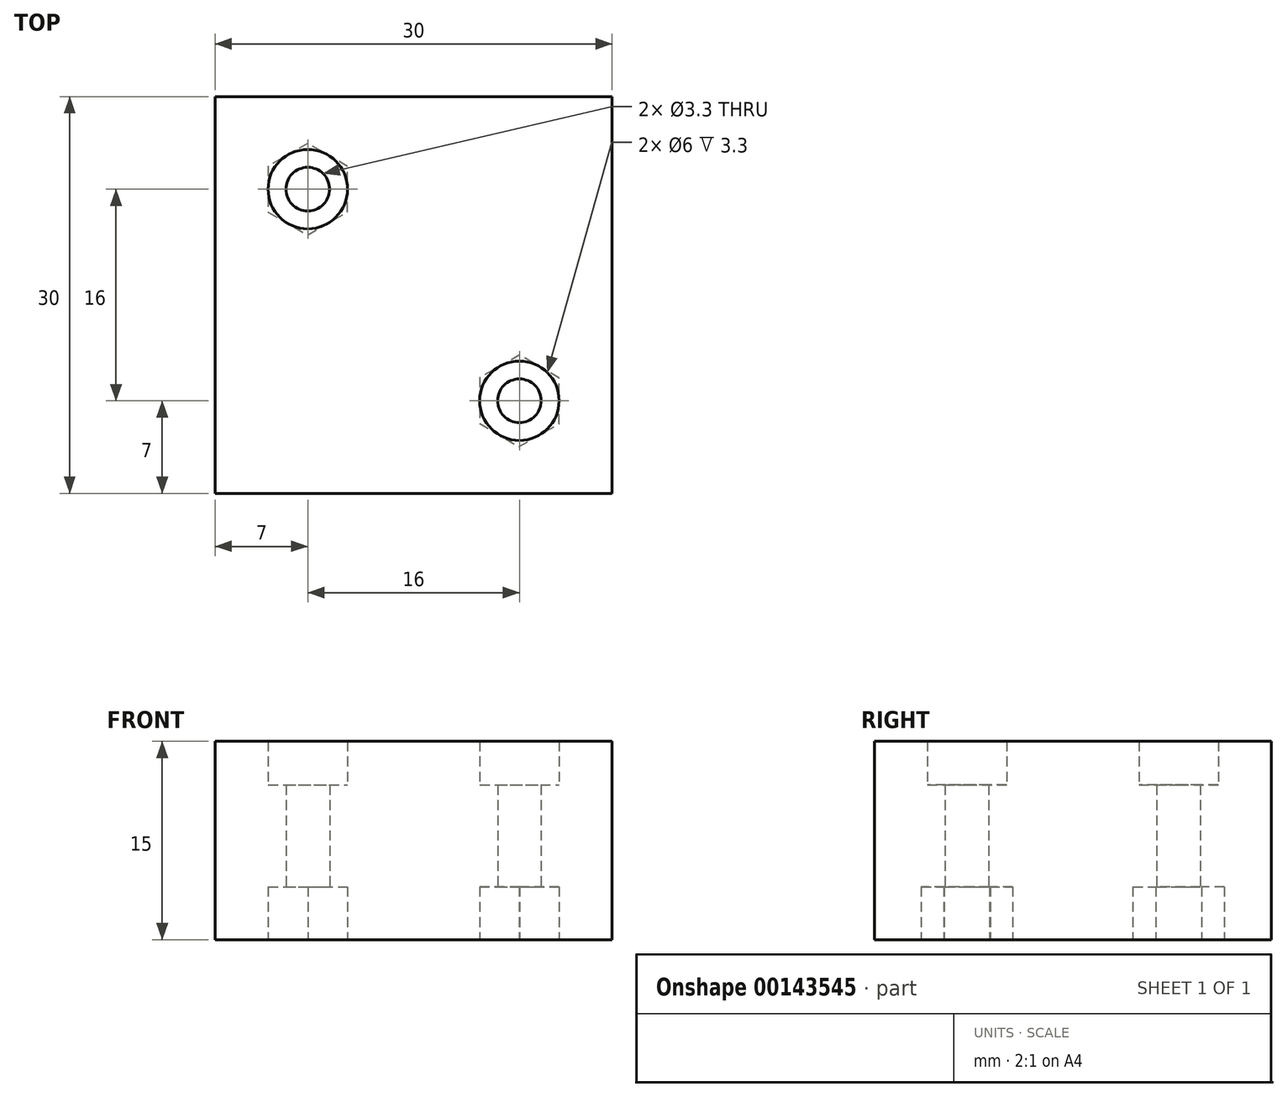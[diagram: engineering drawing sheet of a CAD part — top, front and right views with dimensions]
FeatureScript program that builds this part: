
annotation { "Feature Type Name" : "Feature", "Feature Type Description" : "" }
export const myFeature = defineFeature(function(context is Context, id is Id, definition is map)
    precondition{}
    {
        {
            var Q0;
            Q0=qCreatedBy(makeId("Top.planeOp"),FACE);
            var sketch = newSketch(context, id + "F0", { "sketchPlane" : qUnion([Q0])});
            skLineSegment(sketch, "E0.bottom", {"start": v(-15, 15) * mm, "end": v(15, 15) * mm});
            skLineSegment(sketch, "E0.top", {"start": v(-15, -15) * mm, "end": v(15, -15) * mm});
            skLineSegment(sketch, "E0.left", {"start": v(-15, 15) * mm, "end": v(-15, -15) * mm});
            skLineSegment(sketch, "E0.right", {"start": v(15, 15) * mm, "end": v(15, -15) * mm});
            skSolve(sketch);
        }
        {
            var Q0;
            Q0 = qSketchRegion(id + "F0", true);
            extrude(context, id + "F1", {"entities" : qUnion([Q0]), "depth" : 15 * mm});
        }
        {
            var Q0;
            Q0=makeQuery(id+"F1.opExtrude","CAP_FACE",FACE,{"disambiguationData":[OSD([sQuery(id+"F0.wireOp",EDGE,"E0.bottom"),sQuery(id+"F0.wireOp",EDGE,"E0.top"),sQuery(id+"F0.wireOp",EDGE,"E0.left"),sQuery(id+"F0.wireOp",EDGE,"E0.right")])],"isStart":false});
            var sketch = newSketch(context, id + "F2", { "sketchPlane" : qUnion([Q0])});
            skPoint(sketch, "E1", {"position": v(-8, 8) * mm});
            skPoint(sketch, "E2", {"position": v(8, -8) * mm});
            skSolve(sketch);
        }
        {
            var Q0;
            Q0=sQuery(id+"F2.wireOp",VERTEX,"E1");
            var Q1;
            Q1=sQuery(id+"F2.wireOp",VERTEX,"E2");
            var Q2;
            Q2=makeQuery(id+"F1.opExtrude","SWEPT_BODY",BODY,{"disambiguationData":[OSD([sQuery(id+"F0.wireOp",EDGE,"E0.bottom"),sQuery(id+"F0.wireOp",EDGE,"E0.top"),sQuery(id+"F0.wireOp",EDGE,"E0.left"),sQuery(id+"F0.wireOp",EDGE,"E0.right")])]});
            hole(context, id + "F3", {"style" : HoleStyle.C_BORE, "endStyle" : HoleEndStyle.THROUGH, "holeDiameter" : 3.3 * mm, "cBoreDiameter" : 6 * mm, "cBoreDepth" : 3.3 * mm, "locations" : qUnion([Q0, Q1]), "scope" : qUnion([Q2]), "isTappedThrough" : true, "startStyle" : HoleStartStyle.SKETCH});
        }
        {
            var Q0;
            Q0=makeQuery(id+"F1.opExtrude","CAP_FACE",FACE,{"disambiguationData":[OSD([sQuery(id+"F0.wireOp",EDGE,"E0.bottom"),sQuery(id+"F0.wireOp",EDGE,"E0.top"),sQuery(id+"F0.wireOp",EDGE,"E0.left"),sQuery(id+"F0.wireOp",EDGE,"E0.right")])],"isStart":true});
            var sketch = newSketch(context, id + "F4", { "sketchPlane" : qUnion([Q0])});
            skCircle(sketch, "E3.cCircle", {"center": v(-8, -8) * mm, "radius": 3 * mm, "construction": true});
            skLineSegment(sketch, "E3.0", {"start": v(-5, -6.27) * mm, "end": v(-5, -9.73) * mm});
            skLineSegment(sketch, "E3.1", {"start": v(-5, -9.73) * mm, "end": v(-8, -11.46) * mm});
            skLineSegment(sketch, "E3.2", {"start": v(-8, -11.46) * mm, "end": v(-11, -9.73) * mm});
            skLineSegment(sketch, "E3.3", {"start": v(-11, -9.73) * mm, "end": v(-11, -6.27) * mm});
            skLineSegment(sketch, "E3.4", {"start": v(-11, -6.27) * mm, "end": v(-8, -4.54) * mm});
            skLineSegment(sketch, "E3.5", {"start": v(-8, -4.54) * mm, "end": v(-5, -6.27) * mm});
            skPoint(sketch, "E3.0.midPoint", {"position": v(-5, -8) * mm});
            skCircle(sketch, "E4.cCircle", {"center": v(8, 8) * mm, "radius": 3 * mm, "construction": true});
            skLineSegment(sketch, "E4.0", {"start": v(11.01, 6.3) * mm, "end": v(8.03, 4.54) * mm});
            skLineSegment(sketch, "E4.1", {"start": v(8.03, 4.54) * mm, "end": v(5.01, 6.25) * mm});
            skLineSegment(sketch, "E4.2", {"start": v(5.01, 6.25) * mm, "end": v(4.99, 9.7) * mm});
            skLineSegment(sketch, "E4.3", {"start": v(4.99, 9.7) * mm, "end": v(7.97, 11.46) * mm});
            skLineSegment(sketch, "E4.4", {"start": v(7.97, 11.46) * mm, "end": v(10.99, 9.75) * mm});
            skLineSegment(sketch, "E4.5", {"start": v(10.99, 9.75) * mm, "end": v(11.01, 6.3) * mm});
            skPoint(sketch, "E4.0.midPoint", {"position": v(9.52, 5.41) * mm});
            skSolve(sketch);
        }
        {
            var Q0;
            Q0 = qSketchRegion(id + "F4", true);
            extrude(context, id + "F5", {"entities" : qUnion([Q0]), "operationType" : NewBodyOperationType.REMOVE, "oppositeDirection" : true, "depth" : 4 * mm});
        }
    });
